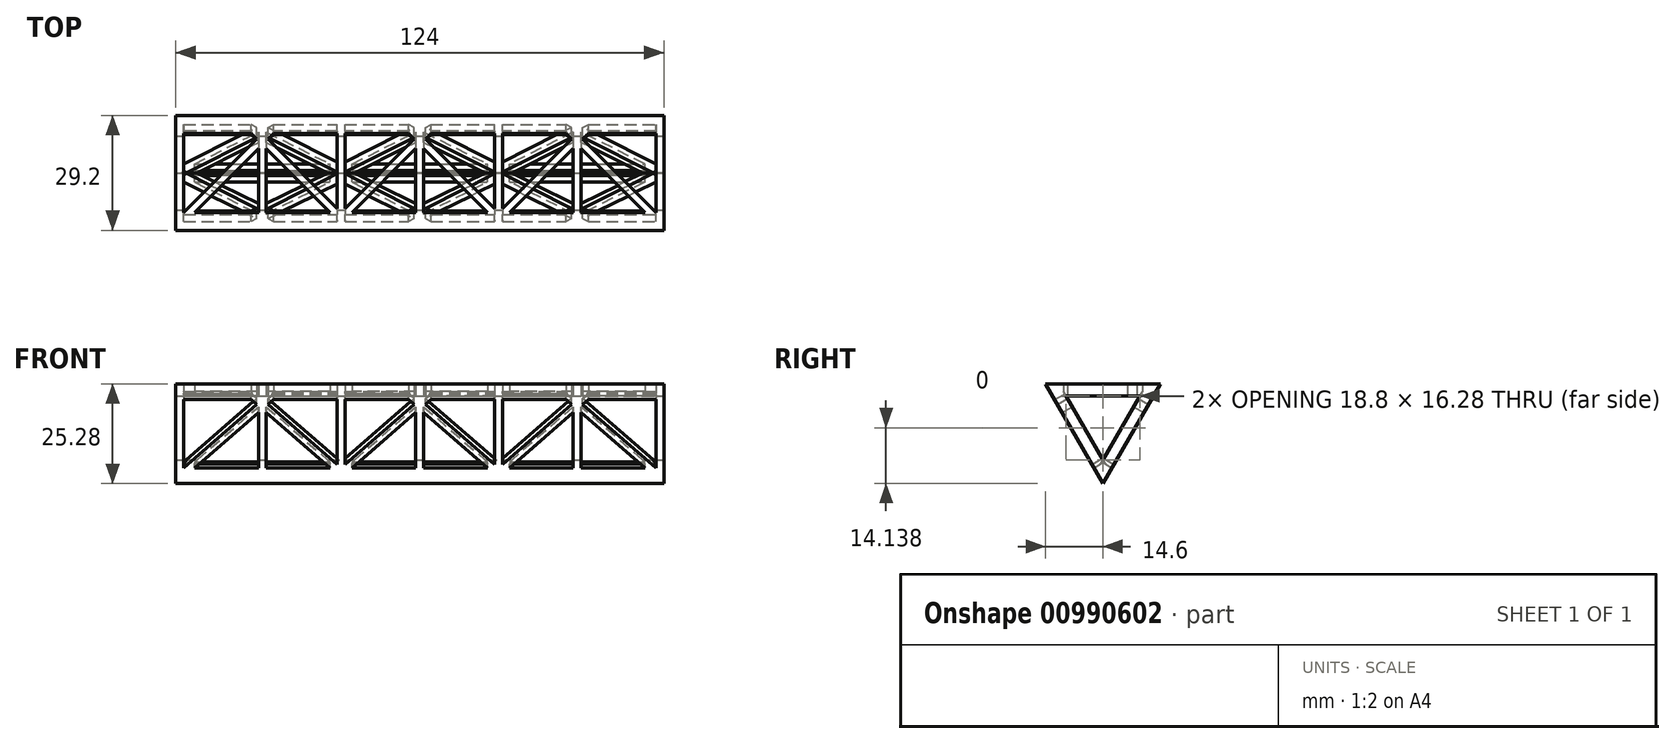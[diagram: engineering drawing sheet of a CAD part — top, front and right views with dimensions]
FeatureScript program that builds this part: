
annotation { "Feature Type Name" : "Feature", "Feature Type Description" : "" }
export const myFeature = defineFeature(function(context is Context, id is Id, definition is map)
    precondition{}
    {
        {
            var Q0;
            Q0=qCreatedBy(makeId("Top.planeOp"),FACE);
            var sketch = newSketch(context, id + "F0", { "sketchPlane" : qUnion([Q0])});
            skLineSegment(sketch, "E0.bottom", {"start": v(-60, 20) * mm, "end": v(60, 20) * mm});
            skLineSegment(sketch, "E0.top", {"start": v(-60, 0) * mm, "end": v(60, 0) * mm});
            skLineSegment(sketch, "E0.left", {"start": v(-60, 20) * mm, "end": v(-60, 0) * mm});
            skLineSegment(sketch, "E0.right", {"start": v(60, 20) * mm, "end": v(60, 0) * mm});
            skLineSegment(sketch, "E1", {"start": v(-60, 0) * mm, "end": v(-40, 20) * mm});
            skLineSegment(sketch, "E2", {"start": v(-40, 20) * mm, "end": v(-20, 0) * mm});
            skLineSegment(sketch, "E3", {"start": v(-20, 0) * mm, "end": v(0, 20) * mm});
            skLineSegment(sketch, "E4", {"start": v(-40, 20) * mm, "end": v(-40, 0) * mm, "construction": true});
            skLineSegment(sketch, "E5", {"start": v(-20, 0) * mm, "end": v(-20, 20) * mm, "construction": true});
            skLineSegment(sketch, "E6.MirrorCS", {"start": v(20, 0) * mm, "end": v(0, 20) * mm});
            skLineSegment(sketch, "E7.MirrorCS", {"start": v(40, 20) * mm, "end": v(20, 0) * mm});
            skLineSegment(sketch, "E8.MirrorCS", {"start": v(60, 0) * mm, "end": v(40, 20) * mm});
            skLineSegment(sketch, "E9", {"start": v(-57.17, 0) * mm, "end": v(-40, 17.17) * mm});
            skLineSegment(sketch, "E10", {"start": v(-40, 17.17) * mm, "end": v(-22.83, 0) * mm});
            skLineSegment(sketch, "E11", {"start": v(-57.17, 0) * mm, "end": v(-60, 0) * mm});
            skLineSegment(sketch, "E12", {"start": v(-22.83, 0) * mm, "end": v(-20, 0) * mm});
            skLineSegment(sketch, "E13", {"start": v(-17.17, 0) * mm, "end": v(0, 17.17) * mm});
            skLineSegment(sketch, "E14", {"start": v(0, 17.17) * mm, "end": v(17.17, 0) * mm});
            skLineSegment(sketch, "E15.MirrorCS", {"start": v(40, 17.17) * mm, "end": v(22.83, 0) * mm});
            skLineSegment(sketch, "E16.MirrorCS", {"start": v(57.17, 0) * mm, "end": v(40, 17.17) * mm});
            skLineSegment(sketch, "E17.0", {"start": v(-62, 22) * mm, "end": v(62, 22) * mm});
            skLineSegment(sketch, "E17.1", {"start": v(-62, 22) * mm, "end": v(-62, -2) * mm});
            skLineSegment(sketch, "E17.2", {"start": v(-62, -2) * mm, "end": v(62, -2) * mm});
            skLineSegment(sketch, "E17.3", {"start": v(62, 22) * mm, "end": v(62, -2) * mm});
            skLineSegment(sketch, "E18", {"start": v(-40, 17.17) * mm, "end": v(-42.83, 20) * mm});
            skLineSegment(sketch, "E19", {"start": v(-42.83, 20) * mm, "end": v(-40, 17.17) * mm});
            skLineSegment(sketch, "E20", {"start": v(-40, 17.17) * mm, "end": v(-37.17, 20) * mm});
            skLineSegment(sketch, "E21.MirrorCS", {"start": v(40, 17.17) * mm, "end": v(37.17, 20) * mm});
            skLineSegment(sketch, "E22.MirrorCS", {"start": v(40, 17.17) * mm, "end": v(42.83, 20) * mm});
            skLineSegment(sketch, "E23", {"start": v(0, 17.17) * mm, "end": v(-2.83, 20) * mm});
            skLineSegment(sketch, "E24.MirrorCS", {"start": v(0, 17.17) * mm, "end": v(2.83, 20) * mm});
            skLineSegment(sketch, "E25.0", {"start": v(-41, 20) * mm, "end": v(-41, 0) * mm});
            skLineSegment(sketch, "E26.0", {"start": v(-39, 20) * mm, "end": v(-39, 0) * mm});
            skLineSegment(sketch, "E27.0", {"start": v(-19, 0) * mm, "end": v(-19, 20) * mm});
            skLineSegment(sketch, "E28.0", {"start": v(-21, 0) * mm, "end": v(-21, 20) * mm});
            skLineSegment(sketch, "E29.MirrorCS", {"start": v(19, 0) * mm, "end": v(19, 20) * mm});
            skLineSegment(sketch, "E30.MirrorCS", {"start": v(21, 0) * mm, "end": v(21, 20) * mm});
            skLineSegment(sketch, "E31.MirrorCS", {"start": v(39, 20) * mm, "end": v(39, 0) * mm});
            skLineSegment(sketch, "E32.MirrorCS", {"start": v(41, 20) * mm, "end": v(41, 0) * mm});
            skLineSegment(sketch, "E33", {"start": v(0, 17.17) * mm, "end": v(0, 0) * mm, "construction": true});
            skLineSegment(sketch, "E34.0", {"start": v(-1, 17.17) * mm, "end": v(-1, 0) * mm});
            skLineSegment(sketch, "E35.MirrorCS", {"start": v(1, 17.17) * mm, "end": v(1, 0) * mm});
            skSolve(sketch);
        }
        {
            var Q0;
            {var subQ33=sQuery(id+"F0.wireOp",EDGE,"E0.left");Q0=makeQuery(id+"F0.imprint","IMPRINT",FACE,{"disambiguationData":[TD([[makeQuery(id+"F0.imprint","IMPRINT",EDGE,{"derivedFrom":subQ33}),-1.0]])]});}
            var Q1;
            {var subQ1=sQuery(id+"F0.wireOp",EDGE,"E10");var subQ3=sQuery(id+"F0.wireOp",EDGE,"E26.0");var subQ4=makeQuery(id+"F0.imprint","INTERSECT",VERTEX,{"derivedFrom":[subQ1,subQ3]});Q1=makeQuery(id+"F0.imprint","IMPRINT",FACE,{"disambiguationData":[TD([[makeQuery(id+"F0.imprint","IMPRINT",EDGE,{"disambiguationData":[TD([[subQ4,1.0]])],"derivedFrom":subQ3}),-1.0]])]});}
            var Q2;
            {var subQ0=sQuery(id+"F0.wireOp",EDGE,"E25.0");var subQ1=sQuery(id+"F0.wireOp",EDGE,"E1");var subQ2=makeQuery(id+"F0.imprint","INTERSECT",VERTEX,{"derivedFrom":[subQ1,subQ0]});Q2=makeQuery(id+"F0.imprint","IMPRINT",FACE,{"disambiguationData":[TD([[makeQuery(id+"F0.imprint","IMPRINT",EDGE,{"disambiguationData":[TD([[subQ2,1.0]])],"derivedFrom":subQ1}),-1.0]])]});}
            var Q3;
            {var subQ0=sQuery(id+"F0.wireOp",EDGE,"E26.0");var subQ1=sQuery(id+"F0.wireOp",EDGE,"E0.bottom");var subQ2=makeQuery(id+"F0.imprint","INTERSECT",VERTEX,{"derivedFrom":[subQ1,subQ0]});Q3=makeQuery(id+"F0.imprint","IMPRINT",FACE,{"disambiguationData":[TD([[makeQuery(id+"F0.imprint","IMPRINT",EDGE,{"disambiguationData":[TD([[subQ2,-1.0]])],"derivedFrom":subQ1}),-1.0]])]});}
            var Q4;
            {var subQ0=sQuery(id+"F0.wireOp",EDGE,"E18");var subQ1=sQuery(id+"F0.wireOp",EDGE,"E0.bottom");var subQ2=makeQuery(id+"F0.imprint","INTERSECT",VERTEX,{"derivedFrom":[subQ1,subQ0]});Q4=makeQuery(id+"F0.imprint","IMPRINT",FACE,{"disambiguationData":[TD([[makeQuery(id+"F0.imprint","IMPRINT",EDGE,{"disambiguationData":[TD([[subQ2,-1.0]])],"derivedFrom":subQ1}),-1.0]])]});}
            var Q5;
            {var subQ1=sQuery(id+"F0.wireOp",EDGE,"E9");var subQ3=sQuery(id+"F0.wireOp",EDGE,"E25.0");var subQ4=makeQuery(id+"F0.imprint","INTERSECT",VERTEX,{"derivedFrom":[subQ1,subQ3]});Q5=makeQuery(id+"F0.imprint","IMPRINT",FACE,{"disambiguationData":[TD([[makeQuery(id+"F0.imprint","IMPRINT",EDGE,{"disambiguationData":[TD([[subQ4,1.0]])],"derivedFrom":subQ3}),1.0]])]});}
            var Q6;
            {var subQ0=sQuery(id+"F0.wireOp",EDGE,"E13");var subQ1=sQuery(id+"F0.wireOp",EDGE,"E0.top");var subQ2=makeQuery(id+"F0.imprint","INTERSECT",VERTEX,{"derivedFrom":[subQ1,subQ0]});Q6=makeQuery(id+"F0.imprint","IMPRINT",FACE,{"disambiguationData":[TD([[makeQuery(id+"F0.imprint","IMPRINT",EDGE,{"disambiguationData":[TD([[subQ2,1.0]])],"derivedFrom":subQ1}),1.0]])]});}
            var Q7;
            {var subQ1=sQuery(id+"F0.wireOp",EDGE,"E3");var subQ3=sQuery(id+"F0.wireOp",EDGE,"E23");var subQ4=makeQuery(id+"F0.imprint","INTERSECT",VERTEX,{"derivedFrom":[subQ1,subQ3]});Q7=makeQuery(id+"F0.imprint","IMPRINT",FACE,{"disambiguationData":[TD([[makeQuery(id+"F0.imprint","IMPRINT",EDGE,{"disambiguationData":[TD([[subQ4,-1.0]])],"derivedFrom":subQ1}),-1.0]])]});}
            var Q8;
            {var subQ0=sQuery(id+"F0.wireOp",EDGE,"E23");var subQ1=sQuery(id+"F0.wireOp",EDGE,"E0.bottom");var subQ2=makeQuery(id+"F0.imprint","INTERSECT",VERTEX,{"derivedFrom":[subQ1,subQ0]});Q8=makeQuery(id+"F0.imprint","IMPRINT",FACE,{"disambiguationData":[TD([[makeQuery(id+"F0.imprint","IMPRINT",EDGE,{"disambiguationData":[TD([[subQ2,1.0]])],"derivedFrom":subQ0}),-1.0]])]});}
            var Q9;
            {var subQ0=sQuery(id+"F0.wireOp",EDGE,"E24.MirrorCS");var subQ3=sQuery(id+"F0.wireOp",EDGE,"E6.MirrorCS");var subQ5=makeQuery(id+"F0.imprint","INTERSECT",VERTEX,{"derivedFrom":[subQ3,subQ0]});Q9=makeQuery(id+"F0.imprint","IMPRINT",FACE,{"disambiguationData":[TD([[makeQuery(id+"F0.imprint","IMPRINT",EDGE,{"disambiguationData":[TD([[subQ5,-1.0]])],"derivedFrom":subQ0}),1.0]])]});}
            var Q10;
            {var subQ1=sQuery(id+"F0.wireOp",EDGE,"E14");var subQ8=sQuery(id+"F0.wireOp",EDGE,"E0.top");var subQ10=makeQuery(id+"F0.imprint","INTERSECT",VERTEX,{"derivedFrom":[subQ8,subQ1]});Q10=makeQuery(id+"F0.imprint","IMPRINT",FACE,{"disambiguationData":[TD([[makeQuery(id+"F0.imprint","IMPRINT",EDGE,{"disambiguationData":[TD([[subQ10,-1.0]])],"derivedFrom":subQ8}),1.0]])]});}
            var Q11;
            {var subQ0=sQuery(id+"F0.wireOp",EDGE,"E31.MirrorCS");var subQ1=sQuery(id+"F0.wireOp",EDGE,"E15.MirrorCS");var subQ2=makeQuery(id+"F0.imprint","INTERSECT",VERTEX,{"derivedFrom":[subQ1,subQ0]});Q11=makeQuery(id+"F0.imprint","IMPRINT",FACE,{"disambiguationData":[TD([[makeQuery(id+"F0.imprint","IMPRINT",EDGE,{"disambiguationData":[TD([[subQ2,1.0]])],"derivedFrom":subQ0}),1.0]])]});}
            var Q12;
            {var subQ0=sQuery(id+"F0.wireOp",EDGE,"E21.MirrorCS");var subQ1=sQuery(id+"F0.wireOp",EDGE,"E7.MirrorCS");var subQ2=makeQuery(id+"F0.imprint","INTERSECT",VERTEX,{"derivedFrom":[subQ1,subQ0]});Q12=makeQuery(id+"F0.imprint","IMPRINT",FACE,{"disambiguationData":[TD([[makeQuery(id+"F0.imprint","IMPRINT",EDGE,{"disambiguationData":[TD([[subQ2,1.0]])],"derivedFrom":subQ1}),1.0]])]});}
            var Q13;
            {var subQ0=sQuery(id+"F0.wireOp",EDGE,"E21.MirrorCS");var subQ1=sQuery(id+"F0.wireOp",EDGE,"E0.bottom");var subQ2=makeQuery(id+"F0.imprint","INTERSECT",VERTEX,{"derivedFrom":[subQ1,subQ0]});Q13=makeQuery(id+"F0.imprint","IMPRINT",FACE,{"disambiguationData":[TD([[makeQuery(id+"F0.imprint","IMPRINT",EDGE,{"disambiguationData":[TD([[subQ2,-1.0]])],"derivedFrom":subQ1}),-1.0]])]});}
            var Q14;
            {var subQ0=sQuery(id+"F0.wireOp",EDGE,"E22.MirrorCS");var subQ1=sQuery(id+"F0.wireOp",EDGE,"E0.bottom");var subQ2=makeQuery(id+"F0.imprint","INTERSECT",VERTEX,{"derivedFrom":[subQ1,subQ0]});Q14=makeQuery(id+"F0.imprint","IMPRINT",FACE,{"disambiguationData":[TD([[makeQuery(id+"F0.imprint","IMPRINT",EDGE,{"disambiguationData":[TD([[subQ2,1.0]])],"derivedFrom":subQ1}),-1.0]])]});}
            var Q15;
            {var subQ1=sQuery(id+"F0.wireOp",EDGE,"E16.MirrorCS");var subQ3=sQuery(id+"F0.wireOp",EDGE,"E32.MirrorCS");var subQ4=makeQuery(id+"F0.imprint","INTERSECT",VERTEX,{"derivedFrom":[subQ1,subQ3]});Q15=makeQuery(id+"F0.imprint","IMPRINT",FACE,{"disambiguationData":[TD([[makeQuery(id+"F0.imprint","IMPRINT",EDGE,{"disambiguationData":[TD([[subQ4,1.0]])],"derivedFrom":subQ3}),-1.0]])]});}
            var Q16;
            {var subQ3=sQuery(id+"F0.wireOp",EDGE,"E25.0");var subQ9=sQuery(id+"F0.wireOp",EDGE,"E1");var subQ11=makeQuery(id+"F0.imprint","INTERSECT",VERTEX,{"derivedFrom":[subQ9,subQ3]});Q16=makeQuery(id+"F0.imprint","IMPRINT",FACE,{"disambiguationData":[TD([[makeQuery(id+"F0.imprint","IMPRINT",EDGE,{"disambiguationData":[TD([[subQ11,-1.0]])],"derivedFrom":subQ3}),1.0]])]});}
            var Q17;
            {var subQ5=sQuery(id+"F0.wireOp",EDGE,"E9");var subQ6=sQuery(id+"F0.wireOp",EDGE,"E0.top");var subQ7=makeQuery(id+"F0.imprint","INTERSECT",VERTEX,{"derivedFrom":[subQ6,subQ5]});Q17=makeQuery(id+"F0.imprint","IMPRINT",FACE,{"disambiguationData":[TD([[makeQuery(id+"F0.imprint","IMPRINT",EDGE,{"disambiguationData":[TD([[subQ7,-1.0]])],"derivedFrom":subQ5}),1.0]])]});}
            var Q18;
            {var subQ3=sQuery(id+"F0.wireOp",EDGE,"E0.top");var subQ7=sQuery(id+"F0.wireOp",EDGE,"E26.0");var subQ8=makeQuery(id+"F0.imprint","INTERSECT",VERTEX,{"derivedFrom":[subQ3,subQ7]});Q18=makeQuery(id+"F0.imprint","IMPRINT",FACE,{"disambiguationData":[TD([[makeQuery(id+"F0.imprint","IMPRINT",EDGE,{"disambiguationData":[TD([[subQ8,1.0]])],"derivedFrom":subQ3}),1.0]])]});}
            var Q19;
            {var subQ7=sQuery(id+"F0.wireOp",EDGE,"E0.top");var subQ9=sQuery(id+"F0.wireOp",EDGE,"E10");var subQ10=makeQuery(id+"F0.imprint","INTERSECT",VERTEX,{"derivedFrom":[subQ7,subQ9]});Q19=makeQuery(id+"F0.imprint","IMPRINT",FACE,{"disambiguationData":[TD([[makeQuery(id+"F0.imprint","IMPRINT",EDGE,{"disambiguationData":[TD([[subQ10,-1.0]])],"derivedFrom":subQ7}),1.0]])]});}
            var Q20;
            {var subQ3=sQuery(id+"F0.wireOp",EDGE,"E0.bottom");var subQ7=sQuery(id+"F0.wireOp",EDGE,"E28.0");var subQ9=makeQuery(id+"F0.imprint","INTERSECT",VERTEX,{"derivedFrom":[subQ3,subQ7]});Q20=makeQuery(id+"F0.imprint","IMPRINT",FACE,{"disambiguationData":[TD([[makeQuery(id+"F0.imprint","IMPRINT",EDGE,{"disambiguationData":[TD([[subQ9,-1.0]])],"derivedFrom":subQ3}),-1.0]])]});}
            var Q21;
            {var subQ0=sQuery(id+"F0.wireOp",EDGE,"E20");var subQ1=sQuery(id+"F0.wireOp",EDGE,"E2");var subQ2=makeQuery(id+"F0.imprint","INTERSECT",VERTEX,{"derivedFrom":[subQ1,subQ0]});Q21=makeQuery(id+"F0.imprint","IMPRINT",FACE,{"disambiguationData":[TD([[makeQuery(id+"F0.imprint","IMPRINT",EDGE,{"disambiguationData":[TD([[subQ2,1.0]])],"derivedFrom":subQ1}),-1.0]])]});}
            var Q22;
            {var subQ0=sQuery(id+"F0.wireOp",EDGE,"E26.0");var subQ1=sQuery(id+"F0.wireOp",EDGE,"E0.bottom");var subQ2=makeQuery(id+"F0.imprint","INTERSECT",VERTEX,{"derivedFrom":[subQ1,subQ0]});Q22=makeQuery(id+"F0.imprint","IMPRINT",FACE,{"disambiguationData":[TD([[makeQuery(id+"F0.imprint","IMPRINT",EDGE,{"disambiguationData":[TD([[subQ2,-1.0]])],"derivedFrom":subQ0}),-1.0]])]});}
            var Q23;
            {var subQ0=sQuery(id+"F0.wireOp",EDGE,"E25.0");var subQ3=sQuery(id+"F0.wireOp",EDGE,"E1");var subQ5=makeQuery(id+"F0.imprint","INTERSECT",VERTEX,{"derivedFrom":[subQ3,subQ0]});Q23=makeQuery(id+"F0.imprint","IMPRINT",FACE,{"disambiguationData":[TD([[makeQuery(id+"F0.imprint","IMPRINT",EDGE,{"disambiguationData":[TD([[subQ5,1.0]])],"derivedFrom":subQ0}),1.0]])]});}
            var Q24;
            {var subQ0=sQuery(id+"F0.wireOp",EDGE,"E27.0");var subQ3=sQuery(id+"F0.wireOp",EDGE,"E3");var subQ5=makeQuery(id+"F0.imprint","INTERSECT",VERTEX,{"derivedFrom":[subQ3,subQ0]});Q24=makeQuery(id+"F0.imprint","IMPRINT",FACE,{"disambiguationData":[TD([[makeQuery(id+"F0.imprint","IMPRINT",EDGE,{"disambiguationData":[TD([[subQ5,1.0]])],"derivedFrom":subQ0}),1.0]])]});}
            var Q25;
            {var subQ0=sQuery(id+"F0.wireOp",EDGE,"E28.0");var subQ3=sQuery(id+"F0.wireOp",EDGE,"E2");var subQ5=makeQuery(id+"F0.imprint","INTERSECT",VERTEX,{"derivedFrom":[subQ3,subQ0]});Q25=makeQuery(id+"F0.imprint","IMPRINT",FACE,{"disambiguationData":[TD([[makeQuery(id+"F0.imprint","IMPRINT",EDGE,{"disambiguationData":[TD([[subQ5,1.0]])],"derivedFrom":subQ0}),-1.0]])]});}
            var Q26;
            {var subQ0=sQuery(id+"F0.wireOp",EDGE,"E29.MirrorCS");var subQ3=sQuery(id+"F0.wireOp",EDGE,"E6.MirrorCS");var subQ5=makeQuery(id+"F0.imprint","INTERSECT",VERTEX,{"derivedFrom":[subQ3,subQ0]});Q26=makeQuery(id+"F0.imprint","IMPRINT",FACE,{"disambiguationData":[TD([[makeQuery(id+"F0.imprint","IMPRINT",EDGE,{"disambiguationData":[TD([[subQ5,1.0]])],"derivedFrom":subQ0}),-1.0]])]});}
            var Q27;
            {var subQ0=sQuery(id+"F0.wireOp",EDGE,"E30.MirrorCS");var subQ1=sQuery(id+"F0.wireOp",EDGE,"E0.top");var subQ2=makeQuery(id+"F0.imprint","INTERSECT",VERTEX,{"derivedFrom":[subQ1,subQ0]});Q27=makeQuery(id+"F0.imprint","IMPRINT",FACE,{"disambiguationData":[TD([[makeQuery(id+"F0.imprint","IMPRINT",EDGE,{"disambiguationData":[TD([[subQ2,-1.0]])],"derivedFrom":subQ0}),1.0]])]});}
            var Q28;
            {var subQ5=sQuery(id+"F0.wireOp",EDGE,"E15.MirrorCS");var subQ6=sQuery(id+"F0.wireOp",EDGE,"E0.top");var subQ7=makeQuery(id+"F0.imprint","INTERSECT",VERTEX,{"derivedFrom":[subQ6,subQ5]});Q28=makeQuery(id+"F0.imprint","IMPRINT",FACE,{"disambiguationData":[TD([[makeQuery(id+"F0.imprint","IMPRINT",EDGE,{"disambiguationData":[TD([[subQ7,1.0]])],"derivedFrom":subQ6}),1.0]])]});}
            var Q29;
            {var subQ0=sQuery(id+"F0.wireOp",EDGE,"E29.MirrorCS");var subQ3=sQuery(id+"F0.wireOp",EDGE,"E0.bottom");var subQ4=makeQuery(id+"F0.imprint","INTERSECT",VERTEX,{"derivedFrom":[subQ3,subQ0]});Q29=makeQuery(id+"F0.imprint","IMPRINT",FACE,{"disambiguationData":[TD([[makeQuery(id+"F0.imprint","IMPRINT",EDGE,{"disambiguationData":[TD([[subQ4,-1.0]])],"derivedFrom":subQ3}),-1.0]])]});}
            var Q30;
            {var subQ0=sQuery(id+"F0.wireOp",EDGE,"E31.MirrorCS");var subQ3=sQuery(id+"F0.wireOp",EDGE,"E0.top");var subQ4=makeQuery(id+"F0.imprint","INTERSECT",VERTEX,{"derivedFrom":[subQ3,subQ0]});Q30=makeQuery(id+"F0.imprint","IMPRINT",FACE,{"disambiguationData":[TD([[makeQuery(id+"F0.imprint","IMPRINT",EDGE,{"disambiguationData":[TD([[subQ4,-1.0]])],"derivedFrom":subQ3}),1.0]])]});}
            var Q31;
            {var subQ5=sQuery(id+"F0.wireOp",EDGE,"E0.top");var subQ7=sQuery(id+"F0.wireOp",EDGE,"E16.MirrorCS");var subQ8=makeQuery(id+"F0.imprint","INTERSECT",VERTEX,{"derivedFrom":[subQ5,subQ7]});Q31=makeQuery(id+"F0.imprint","IMPRINT",FACE,{"disambiguationData":[TD([[makeQuery(id+"F0.imprint","IMPRINT",EDGE,{"disambiguationData":[TD([[subQ8,-1.0]])],"derivedFrom":subQ7}),-1.0]])]});}
            var Q32;
            {var subQ0=sQuery(id+"F0.wireOp",EDGE,"E31.MirrorCS");var subQ1=sQuery(id+"F0.wireOp",EDGE,"E0.bottom");var subQ2=makeQuery(id+"F0.imprint","INTERSECT",VERTEX,{"derivedFrom":[subQ1,subQ0]});Q32=makeQuery(id+"F0.imprint","IMPRINT",FACE,{"disambiguationData":[TD([[makeQuery(id+"F0.imprint","IMPRINT",EDGE,{"disambiguationData":[TD([[subQ2,-1.0]])],"derivedFrom":subQ0}),1.0]])]});}
            var Q33;
            {var subQ0=sQuery(id+"F0.wireOp",EDGE,"E32.MirrorCS");var subQ3=sQuery(id+"F0.wireOp",EDGE,"E8.MirrorCS");var subQ5=makeQuery(id+"F0.imprint","INTERSECT",VERTEX,{"derivedFrom":[subQ3,subQ0]});Q33=makeQuery(id+"F0.imprint","IMPRINT",FACE,{"disambiguationData":[TD([[makeQuery(id+"F0.imprint","IMPRINT",EDGE,{"disambiguationData":[TD([[subQ5,1.0]])],"derivedFrom":subQ0}),-1.0]])]});}
            var Q34;
            {var subQ0=sQuery(id+"F0.wireOp",EDGE,"E32.MirrorCS");var subQ1=sQuery(id+"F0.wireOp",EDGE,"E8.MirrorCS");var subQ2=makeQuery(id+"F0.imprint","INTERSECT",VERTEX,{"derivedFrom":[subQ1,subQ0]});Q34=makeQuery(id+"F0.imprint","IMPRINT",FACE,{"disambiguationData":[TD([[makeQuery(id+"F0.imprint","IMPRINT",EDGE,{"disambiguationData":[TD([[subQ2,1.0]])],"derivedFrom":subQ1}),1.0]])]});}
            var Q35;
            {var subQ1=sQuery(id+"F0.wireOp",EDGE,"E21.MirrorCS");var subQ5=sQuery(id+"F0.wireOp",EDGE,"E31.MirrorCS");var subQ6=makeQuery(id+"F0.imprint","INTERSECT",VERTEX,{"derivedFrom":[subQ1,subQ5]});Q35=makeQuery(id+"F0.imprint","IMPRINT",FACE,{"disambiguationData":[TD([[makeQuery(id+"F0.imprint","IMPRINT",EDGE,{"disambiguationData":[TD([[subQ6,1.0]])],"derivedFrom":subQ5}),1.0]])]});}
            var Q36;
            {var subQ0=sQuery(id+"F0.wireOp",EDGE,"E34.0");var subQ3=sQuery(id+"F0.wireOp",EDGE,"E0.top");var subQ4=makeQuery(id+"F0.imprint","INTERSECT",VERTEX,{"derivedFrom":[subQ3,subQ0]});Q36=makeQuery(id+"F0.imprint","IMPRINT",FACE,{"disambiguationData":[TD([[makeQuery(id+"F0.imprint","IMPRINT",EDGE,{"disambiguationData":[TD([[subQ4,-1.0]])],"derivedFrom":subQ3}),1.0]])]});}
            extrude(context, id + "F1", {"entities" : qUnion([Q0, Q1, Q2, Q3, Q4, Q5, Q6, Q7, Q8, Q9, Q10, Q11, Q12, Q13, Q14, Q15, Q16, Q17, Q18, Q19, Q20, Q21, Q22, Q23, Q24, Q25, Q26, Q27, Q28, Q29, Q30, Q31, Q32, Q33, Q34, Q35, Q36]), "depth" : 3 * mm, "offsetDistance" : 25 * mm});
        }
        {
            var Q0;
            Q0=qCreatedBy(makeId("Right.planeOp"),FACE);
            var sketch = newSketch(context, id + "F2", { "sketchPlane" : qUnion([Q0])});
            skCircle(sketch, "E36", {"center": v(0, 10) * mm, "radius": 10 * mm});
            skLineSegment(sketch, "E37", {"start": v(22, 0) * mm, "end": v(12, 17.32) * mm});
            skLineSegment(sketch, "E38", {"start": v(12, 17.32) * mm, "end": v(0, 0) * mm});
            skCircle(sketch, "E39", {"center": v(22, 1.5) * mm, "radius": 10 * mm});
            skSolve(sketch);
        }
        {
            var Q0;
            Q0=makeQuery(id+"F1.opExtrude","SWEPT_BODY",BODY,{"disambiguationData":[OSD([sQuery(id+"F0.wireOp",EDGE,"E0.bottom"),sQuery(id+"F0.wireOp",EDGE,"E0.top"),sQuery(id+"F0.wireOp",EDGE,"E0.left"),sQuery(id+"F0.wireOp",EDGE,"E0.right"),sQuery(id+"F0.wireOp",EDGE,"E1"),sQuery(id+"F0.wireOp",EDGE,"E2"),sQuery(id+"F0.wireOp",EDGE,"E3"),sQuery(id+"F0.wireOp",EDGE,"E6.MirrorCS"),sQuery(id+"F0.wireOp",EDGE,"E7.MirrorCS"),sQuery(id+"F0.wireOp",EDGE,"E8.MirrorCS"),sQuery(id+"F0.wireOp",EDGE,"E9"),sQuery(id+"F0.wireOp",EDGE,"E10"),sQuery(id+"F0.wireOp",EDGE,"E13"),sQuery(id+"F0.wireOp",EDGE,"E14"),sQuery(id+"F0.wireOp",EDGE,"E15.MirrorCS"),sQuery(id+"F0.wireOp",EDGE,"E16.MirrorCS"),sQuery(id+"F0.wireOp",EDGE,"E17.0"),sQuery(id+"F0.wireOp",EDGE,"E17.1"),sQuery(id+"F0.wireOp",EDGE,"E17.2"),sQuery(id+"F0.wireOp",EDGE,"E17.3"),sQuery(id+"F0.wireOp",EDGE,"E18"),sQuery(id+"F0.wireOp",EDGE,"E20"),sQuery(id+"F0.wireOp",EDGE,"E21.MirrorCS"),sQuery(id+"F0.wireOp",EDGE,"E22.MirrorCS"),sQuery(id+"F0.wireOp",EDGE,"E23"),sQuery(id+"F0.wireOp",EDGE,"E24.MirrorCS"),sQuery(id+"F0.wireOp",EDGE,"E25.0"),sQuery(id+"F0.wireOp",EDGE,"E26.0"),sQuery(id+"F0.wireOp",EDGE,"E27.0"),sQuery(id+"F0.wireOp",EDGE,"E28.0"),sQuery(id+"F0.wireOp",EDGE,"E29.MirrorCS"),sQuery(id+"F0.wireOp",EDGE,"E30.MirrorCS"),sQuery(id+"F0.wireOp",EDGE,"E31.MirrorCS"),sQuery(id+"F0.wireOp",EDGE,"E32.MirrorCS"),sQuery(id+"F0.wireOp",EDGE,"E34.0"),sQuery(id+"F0.wireOp",EDGE,"E35.MirrorCS")])]});
            var Q1;
            Q1=sQuery(id+"F2.wireOp",EDGE,"E39");
            circularPattern(context, id + "F3", {"entities" : qUnion([Q0]), "axis" : qUnion([Q1]), "angle" : 60 * degree, "instanceCount" : 2, "equalSpace" : true});
        }
        {
            var Q0;
            {var subQ0=makeQuery(id+"F1.opExtrude","SWEPT_FACE",FACE,{"disambiguationData":[OSD([sQuery(id+"F0.wireOp",EDGE,"E17.1")])]});Q0=qUnion([subQ0,makeQuery(id+"F3.opPattern","COPY",FACE,{"derivedFrom":subQ0,"instanceName":"1"})]);}
            var sketch = newSketch(context, id + "F4", { "sketchPlane" : qUnion([Q0])});
            skCircle(sketch, "E40", {"center": v(-10, -19.28) * mm, "radius": 10 * mm});
            skSolve(sketch);
        }
        {
            var Q0;
            Q0=makeQuery(id+"F3.opPattern","COPY",BODY,{"derivedFrom":makeQuery(id+"F1.opExtrude","SWEPT_BODY",BODY,{"disambiguationData":[OSD([sQuery(id+"F0.wireOp",EDGE,"E0.bottom"),sQuery(id+"F0.wireOp",EDGE,"E0.top"),sQuery(id+"F0.wireOp",EDGE,"E0.left"),sQuery(id+"F0.wireOp",EDGE,"E0.right"),sQuery(id+"F0.wireOp",EDGE,"E1"),sQuery(id+"F0.wireOp",EDGE,"E2"),sQuery(id+"F0.wireOp",EDGE,"E3"),sQuery(id+"F0.wireOp",EDGE,"E6.MirrorCS"),sQuery(id+"F0.wireOp",EDGE,"E7.MirrorCS"),sQuery(id+"F0.wireOp",EDGE,"E8.MirrorCS"),sQuery(id+"F0.wireOp",EDGE,"E9"),sQuery(id+"F0.wireOp",EDGE,"E10"),sQuery(id+"F0.wireOp",EDGE,"E13"),sQuery(id+"F0.wireOp",EDGE,"E14"),sQuery(id+"F0.wireOp",EDGE,"E15.MirrorCS"),sQuery(id+"F0.wireOp",EDGE,"E16.MirrorCS"),sQuery(id+"F0.wireOp",EDGE,"E17.0"),sQuery(id+"F0.wireOp",EDGE,"E17.1"),sQuery(id+"F0.wireOp",EDGE,"E17.2"),sQuery(id+"F0.wireOp",EDGE,"E17.3"),sQuery(id+"F0.wireOp",EDGE,"E18"),sQuery(id+"F0.wireOp",EDGE,"E20"),sQuery(id+"F0.wireOp",EDGE,"E21.MirrorCS"),sQuery(id+"F0.wireOp",EDGE,"E22.MirrorCS"),sQuery(id+"F0.wireOp",EDGE,"E23"),sQuery(id+"F0.wireOp",EDGE,"E24.MirrorCS"),sQuery(id+"F0.wireOp",EDGE,"E25.0"),sQuery(id+"F0.wireOp",EDGE,"E26.0"),sQuery(id+"F0.wireOp",EDGE,"E27.0"),sQuery(id+"F0.wireOp",EDGE,"E28.0"),sQuery(id+"F0.wireOp",EDGE,"E29.MirrorCS"),sQuery(id+"F0.wireOp",EDGE,"E30.MirrorCS"),sQuery(id+"F0.wireOp",EDGE,"E31.MirrorCS"),sQuery(id+"F0.wireOp",EDGE,"E32.MirrorCS"),sQuery(id+"F0.wireOp",EDGE,"E34.0"),sQuery(id+"F0.wireOp",EDGE,"E35.MirrorCS")])]}),"instanceName":"1"});
            var Q1;
            Q1=sQuery(id+"F4.wireOp",EDGE,"E40");
            circularPattern(context, id + "F5", {"operationType" : NewBodyOperationType.ADD, "entities" : qUnion([Q0]), "axis" : qUnion([Q1]), "angle" : 60 * degree, "instanceCount" : 2, "oppositeDirection" : true, "equalSpace" : true});
        }
        {
            var Q0;
            {var subQ0=makeQuery(id+"F1.opExtrude","SWEPT_FACE",FACE,{"disambiguationData":[OSD([sQuery(id+"F0.wireOp",EDGE,"E17.1")])]});var subQ1=makeQuery(id+"F3.opPattern","COPY",FACE,{"derivedFrom":subQ0,"instanceName":"1"});Q0=makeQuery(id+"F5.boolean.opBoolean","MERGE",FACE,{"derivedFrom":[subQ0,subQ1,makeQuery(id+"F5.opPattern","COPY",FACE,{"derivedFrom":subQ1,"instanceName":"1"})]});}
            var sketch = newSketch(context, id + "F6", { "sketchPlane" : qUnion([Q0])});
            skLineSegment(sketch, "E41", {"start": v(-23.3, 0.75) * mm, "end": v(-25.92, 5.3) * mm});
            skLineSegment(sketch, "E42", {"start": v(-22, 3) * mm, "end": v(-28.13, 3) * mm});
            skLineSegment(sketch, "E43", {"start": v(2, 3) * mm, "end": v(9.43, 3) * mm});
            skLineSegment(sketch, "E44", {"start": v(3.3, 0.75) * mm, "end": v(6.8, 6.8) * mm});
            skLineSegment(sketch, "E45", {"start": v(-8.7, -20.03) * mm, "end": v(-11.3, -24.53) * mm});
            skLineSegment(sketch, "E46", {"start": v(-11.3, -20.03) * mm, "end": v(-7.1, -27.3) * mm});
            skSolve(sketch);
        }
        {
            var Q0;
            {var subQ1=sQuery(id+"F0.wireOp",EDGE,"E17.1");var subQ2=makeQuery(id+"F1.opExtrude","SWEPT_EDGE",EDGE,{"disambiguationData":[OSD([sQuery(id+"F0.wireOp",EDGE,"E17.0"),subQ1])]});var subQ6=subQ2;Q0=makeQuery(id+"F6.imprint","IMPRINT",FACE,{"disambiguationData":[TD([[makeQuery(id+"F6.imprint","IMPRINT",EDGE,{"derivedFrom":subQ6}),-1.0]])]});}
            var Q1;
            {var subQ1=sQuery(id+"F0.wireOp",EDGE,"E17.1");var subQ2=makeQuery(id+"F1.opExtrude","SWEPT_EDGE",EDGE,{"disambiguationData":[OSD([subQ1,sQuery(id+"F0.wireOp",EDGE,"E17.2")])]});Q1=makeQuery(id+"F6.imprint","IMPRINT",FACE,{"disambiguationData":[TD([[makeQuery(id+"F6.imprint","IMPRINT",EDGE,{"derivedFrom":subQ2}),1.0]])]});}
            var Q2;
            {var subQ1=sQuery(id+"F0.wireOp",EDGE,"E17.1");var subQ2=makeQuery(id+"F3.opPattern","COPY",EDGE,{"derivedFrom":makeQuery(id+"F1.opExtrude","SWEPT_EDGE",EDGE,{"disambiguationData":[OSD([subQ1,sQuery(id+"F0.wireOp",EDGE,"E17.2")])]}),"instanceName":"1"});var subQ6=subQ2;Q2=makeQuery(id+"F6.imprint","IMPRINT",FACE,{"disambiguationData":[TD([[makeQuery(id+"F6.imprint","IMPRINT",EDGE,{"derivedFrom":subQ6}),1.0]])]});}
            extrude(context, id + "F7", {"entities" : qUnion([Q0, Q1, Q2]), "operationType" : NewBodyOperationType.ADD, "oppositeDirection" : true, "depth" : 124 * mm, "offsetDistance" : 25 * mm});
        }
    });
